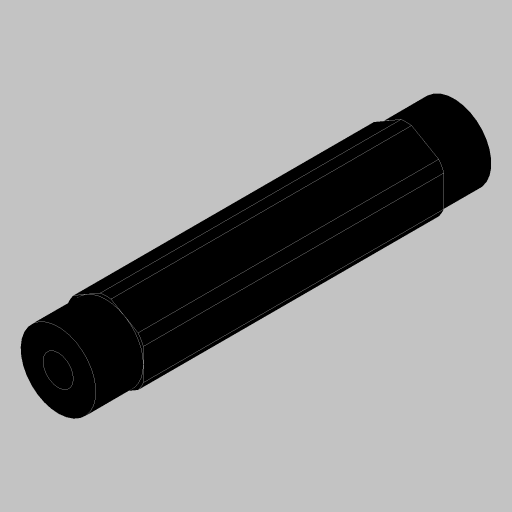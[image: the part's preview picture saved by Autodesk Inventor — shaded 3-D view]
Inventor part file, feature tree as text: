
AUTODESK INVENTOR PART (.ipt)
format: ipt  version: 2023.5 (Build 275446000, 446)  size: 164,864 bytes
history: native  units: in
note: dims shown in document units (in); Inventor stores cm internally (conversion verified against a paired STEP export)
features: extrude x3, projected_geometry x3, hole x1, mirror x1, sketch x1
ambient origin geometry x8: Origin, YZ Plane, XZ Plane, XY Plane, X Axis, Y Axis, Z Axis, Center Point
bodies: Solid1 (feature_tree)
feature tree (9):
  extrude  "Extrusion1"  Depth=0.315in
  hole  "Hole1"  [1 undecoded]
  extrude  "Extrusion3"  Depth=0.5in
  extrude  "Extrusion4"  Depth=0.315in TaperAngle=0.0deg
  mirror  "Mirror2"
  sketch  "Sketch5"  dims[d2=0.0in d9=0.625in d10=0.385in d11=0.25in d12=0.5635in d13=1.0in d14=0.8108in d16=0.7in d17=0.0in d18=0.0in d19=0.5in d20=0.315in d21=0.0in]
  projected_geometry  "Projected Loop2"
  projected_geometry  "Project Cut Edges1"
  projected_geometry  "Project Cut Edges2"
note: 1 required parameter value undecoded (feature->parameter linkage not recoverable at this tier; creation-order binding heuristic only, values carry confidence <= 0.55)
